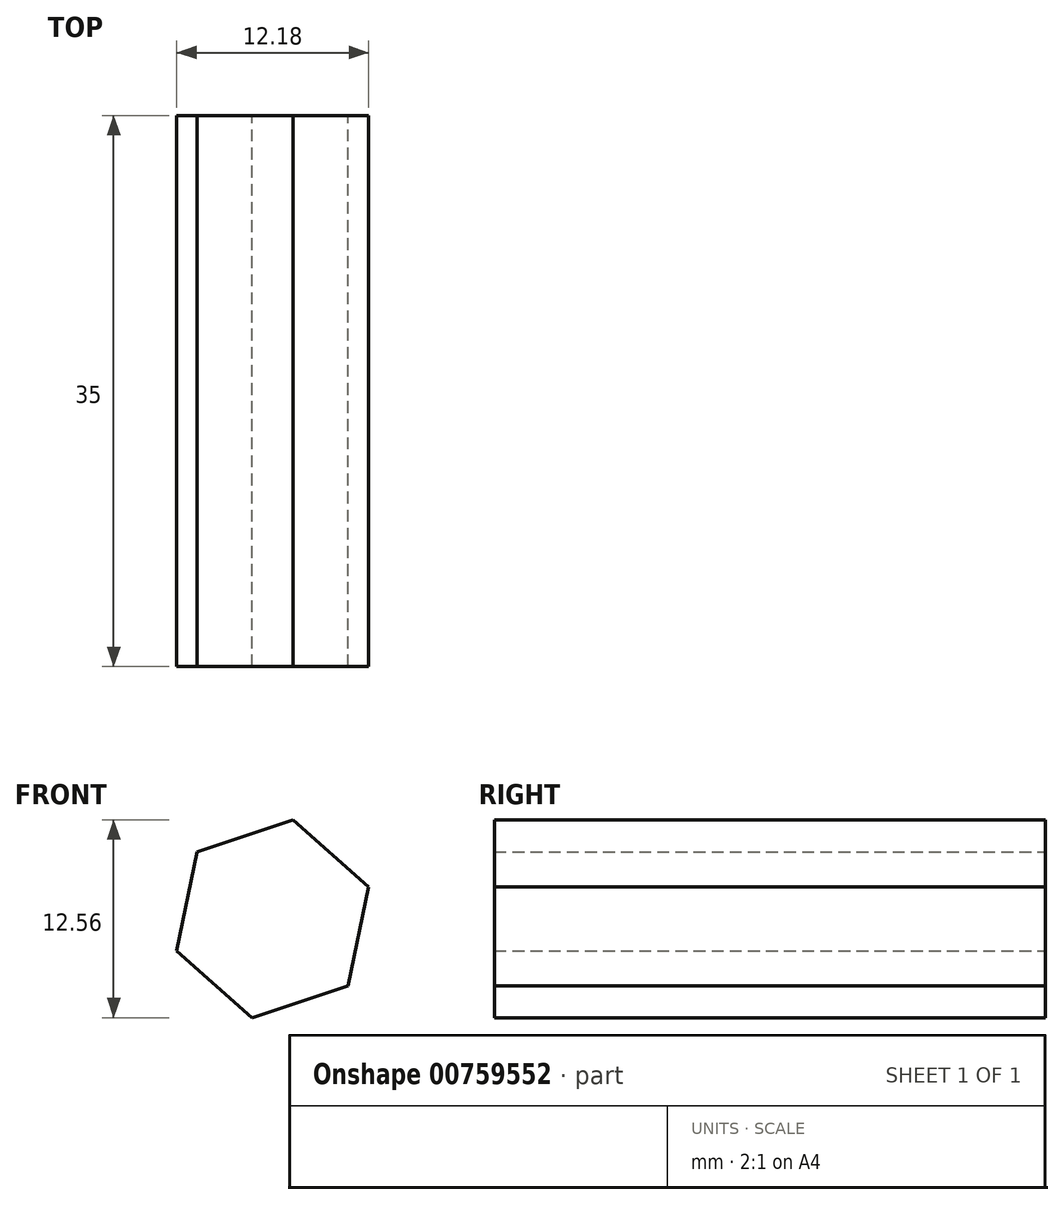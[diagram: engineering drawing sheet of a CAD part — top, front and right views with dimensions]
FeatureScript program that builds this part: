
annotation { "Feature Type Name" : "Feature", "Feature Type Description" : "" }
export const myFeature = defineFeature(function(context is Context, id is Id, definition is map)
    precondition{}
    {
        {
            var Q0;
            Q0=qCreatedBy(makeId("Front.planeOp"),FACE);
            var sketch = newSketch(context, id + "F0", { "sketchPlane" : qUnion([Q0])});
            skCircle(sketch, "E0.cCircle", {"center": v(0, 0) * mm, "radius": 5.55 * mm, "construction": true});
            skLineSegment(sketch, "E0.0", {"start": v(1.3, 6.28) * mm, "end": v(6.09, 2.02) * mm});
            skLineSegment(sketch, "E0.1", {"start": v(6.09, 2.02) * mm, "end": v(4.8, -4.26) * mm});
            skLineSegment(sketch, "E0.2", {"start": v(4.8, -4.26) * mm, "end": v(-1.3, -6.28) * mm});
            skLineSegment(sketch, "E0.3", {"start": v(-1.3, -6.28) * mm, "end": v(-6.09, -2.02) * mm});
            skLineSegment(sketch, "E0.4", {"start": v(-6.09, -2.02) * mm, "end": v(-4.8, 4.26) * mm});
            skLineSegment(sketch, "E0.5", {"start": v(-4.8, 4.26) * mm, "end": v(1.3, 6.28) * mm});
            skPoint(sketch, "E0.0.midPoint", {"position": v(3.69, 4.15) * mm});
            skSolve(sketch);
        }
        {
            var Q0;
            Q0 = qSketchRegion(id + "F0", true);
            extrude(context, id + "F1", {"entities" : qUnion([Q0]), "depth" : 35 * mm, "offsetDistance" : 25 * mm});
        }
    });
